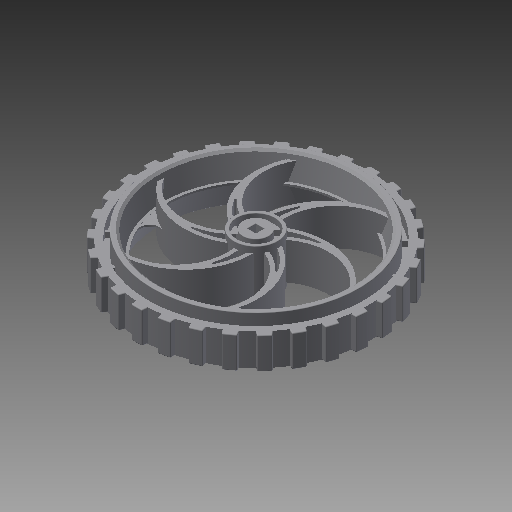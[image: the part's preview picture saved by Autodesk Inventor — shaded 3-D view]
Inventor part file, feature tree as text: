
AUTODESK INVENTOR PART (.ipt)
format: ipt  version: 2018 (Build 220112000, 112)  size: 1,253,376 bytes
history: native  units: mm (DEFAULTED — no unit token found)
features: imported_body x1, sketch x1, other x1, extrude x1
ambient origin geometry x8: Origin, YZ Plane, XZ Plane, XY Plane, X Axis, Y Axis, Z Axis, Center Point
bodies: Solid1 (feature_tree)
feature tree (4):
  imported_body  "Base1"
  sketch  "Sketch1"  dims[d0=25.4mm d1=0.0mm d2=0.0mm d3=0.0mm]
  other  "Srf1"
  extrude  "ExtrusionSrf1"  TaperAngle=0.0deg  [1 undecoded]
note: 1 required parameter value undecoded (feature->parameter linkage not recoverable at this tier; creation-order binding heuristic only, values carry confidence <= 0.55)
